# Revit family: Toilet_Tissue_Dispenser-Bradley_Corp-Coreless_Jumbo_Dual_Roll_Surface_Mount-5426-11
name_source: partatom
category: Specialty Equipment
revit_build: Autodesk Revit 2018 (Build: 20170223_1515(x64)
units: mm (PartAtom-declared; Revit-internal decimal feet)

## family parameters
Cut with Voids When Loaded = No
Host = Face
Part Type = Normal
Room Calculation Point = No
Round Connector Dimension = Use Diameter
Shared = No

## types (1)
- 5426-11
    5952 Paper Roll Visibility = No
    ADA Compliant = Yes
    Assembly Code = C1030200
    Buy American Act = To Be Determined
    Default Elevation = 0.000"
    Depth = 6.188"
    Description = Toilet Tissue Dispenser - Coreless Jumbo Dual Roll
    Height = 11.375"
    Low Emitting Material = No
    Manufacturer = Bradley Corporation
    MasterFormat Number = 10 28 00
    MasterFormat Title = Toilet, Bath, and Laundry Accessories
    Model = 5426-11
    OmniClass Code = 23.31.25.21
    OmniClass Title = Toilet Paper Dispensers
    Percentage of Recycled Content = 0
    Product Page URL = https://www.bradleycorp.com
    Product Tech Data URL - English = https://www.bradleycorp.com
    URL = http://www.bradleycorp.com
    Unit Material = Metal - Bradley Corp - Stainless Steel - Satin
    Version = 1.0
    Warranty Information = Complete Unit 1 Year Warranty. This Warranty does not cover installation or any other labor charges and does not apply to any units which have been damaged by abuse, improper installation, imporper maintanence, or altered in any way.
    Width = 21.000"

## geometry (parser evidence)
native form markers: Sweep x2
no freeform markers — native parametric forms only
